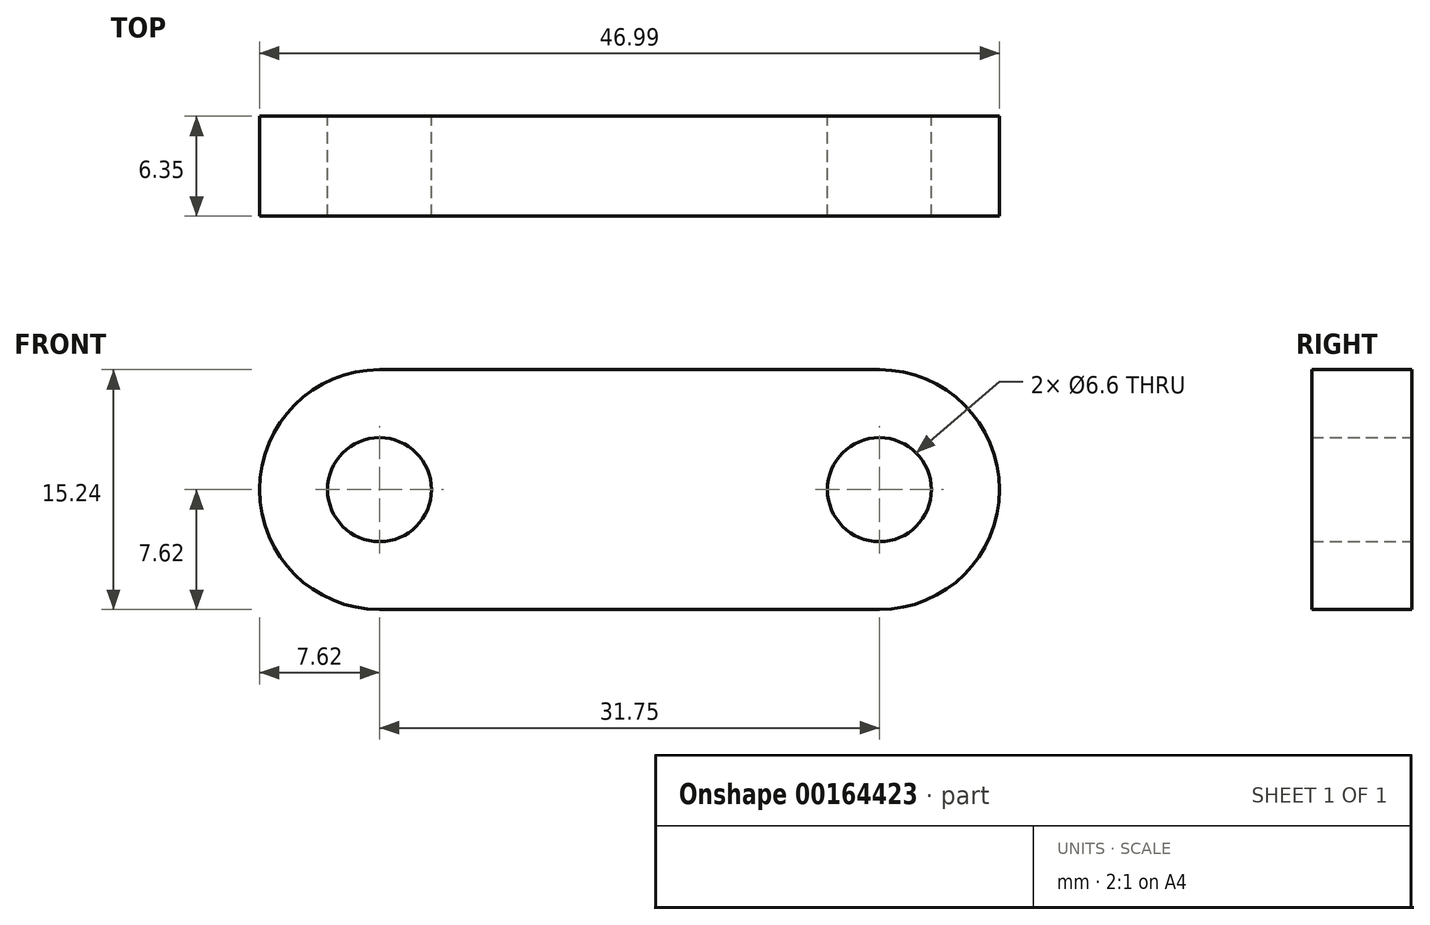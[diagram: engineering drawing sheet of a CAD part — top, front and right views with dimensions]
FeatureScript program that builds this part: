
annotation { "Feature Type Name" : "Feature", "Feature Type Description" : "" }
export const myFeature = defineFeature(function(context is Context, id is Id, definition is map)
    precondition{}
    {
        {
            var Q0;
            Q0=qCreatedBy(makeId("Front.planeOp"),FACE);
            var sketch = newSketch(context, id + "F0", { "sketchPlane" : qUnion([Q0])});
            skCircle(sketch, "E0", {"center": v(0, 0) * mm, "radius": 3.3 * mm});
            skCircle(sketch, "E1", {"center": v(31.75, 0) * mm, "radius": 3.3 * mm});
            skArc(sketch, "E2", {"start": v(0, 7.62) * mm, "mid": v(-7.62, 0) * mm, "end": v(0, -7.62) * mm});
            skArc(sketch, "E3", {"start": v(31.75, -7.62) * mm, "mid": v(39.37, 0) * mm, "end": v(31.75, 7.62) * mm});
            skLineSegment(sketch, "E4", {"start": v(0, 7.62) * mm, "end": v(31.75, 7.62) * mm});
            skLineSegment(sketch, "E5", {"start": v(31.75, -7.62) * mm, "end": v(0, -7.62) * mm});
            skSolve(sketch);
        }
        {
            var Q0;
            Q0=makeQuery(id+"F0.imprint","IMPRINT",FACE,{"disambiguationData":[TD([[makeQuery(id+"F0.imprint","IMPRINT",EDGE,{"derivedFrom":sQuery(id+"F0.wireOp",EDGE,"E0")}),-1.0]])]});
            extrude(context, id + "F1", {"entities" : qUnion([Q0]), "depth" : 6.35 * mm});
        }
    });
